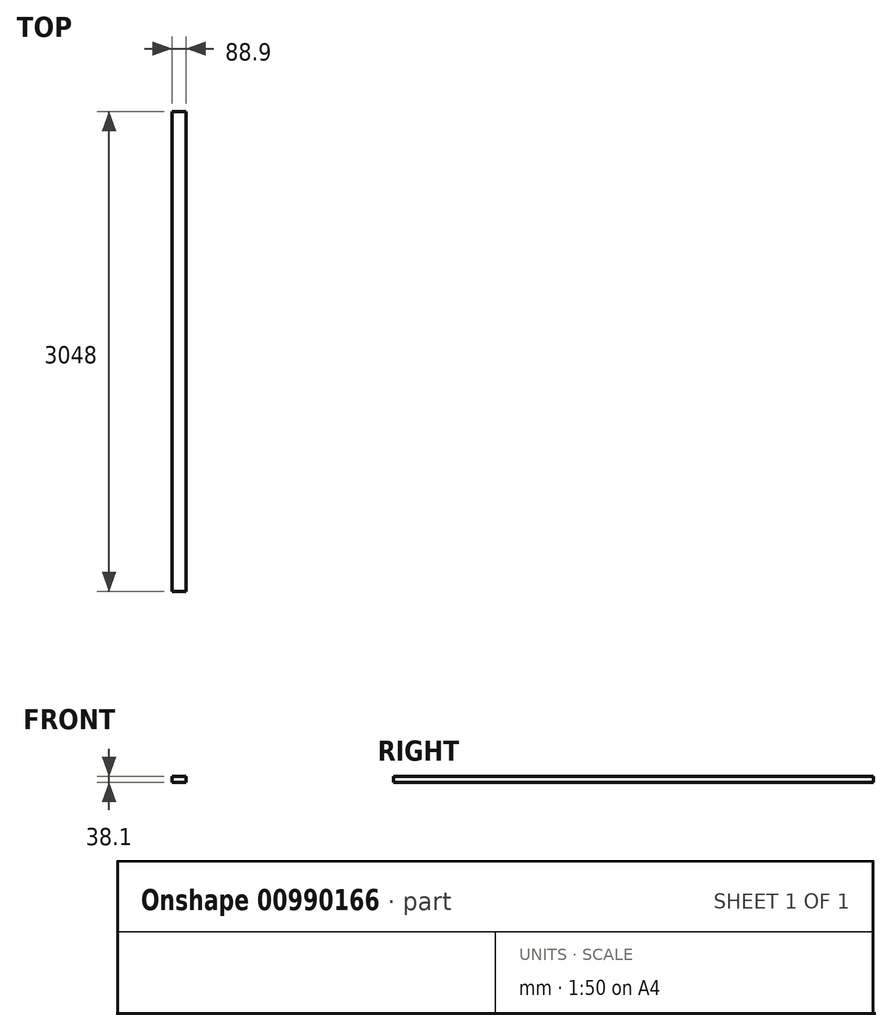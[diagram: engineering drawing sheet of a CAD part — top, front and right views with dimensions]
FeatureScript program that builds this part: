
annotation { "Feature Type Name" : "Feature", "Feature Type Description" : "" }
export const myFeature = defineFeature(function(context is Context, id is Id, definition is map)
    precondition{}
    {
        {
            assignVariable(context, id + "F0", {"name" : "w", "anyValue" : 38.1 * mm});
        }
        {
            var Q0;
            Q0=qCreatedBy(makeId("Top.planeOp"),FACE);
            var sketch = newSketch(context, id + "F1", { "sketchPlane" : qUnion([Q0])});
            skLineSegment(sketch, "E0.bottom", {"start": v(44.45, 1524) * mm, "end": v(-44.45, 1524) * mm});
            skLineSegment(sketch, "E0.top", {"start": v(44.45, -1524) * mm, "end": v(-44.45, -1524) * mm});
            skLineSegment(sketch, "E0.left", {"start": v(44.45, 1524) * mm, "end": v(44.45, -1524) * mm});
            skLineSegment(sketch, "E0.right", {"start": v(-44.45, 1524) * mm, "end": v(-44.45, -1524) * mm});
            skPoint(sketch, "E0.middle", {"position": v(0, 0) * mm});
            skSolve(sketch);
        }
        {
            var Q0;
            Q0=qSketchRegion(id+"F1",true);
            extrude(context, id + "F2", {"entities" : qUnion([Q0]), "depth" : getVariable(context, 'w'), "offsetDistance" : 25.4 * mm});
        }
    });
